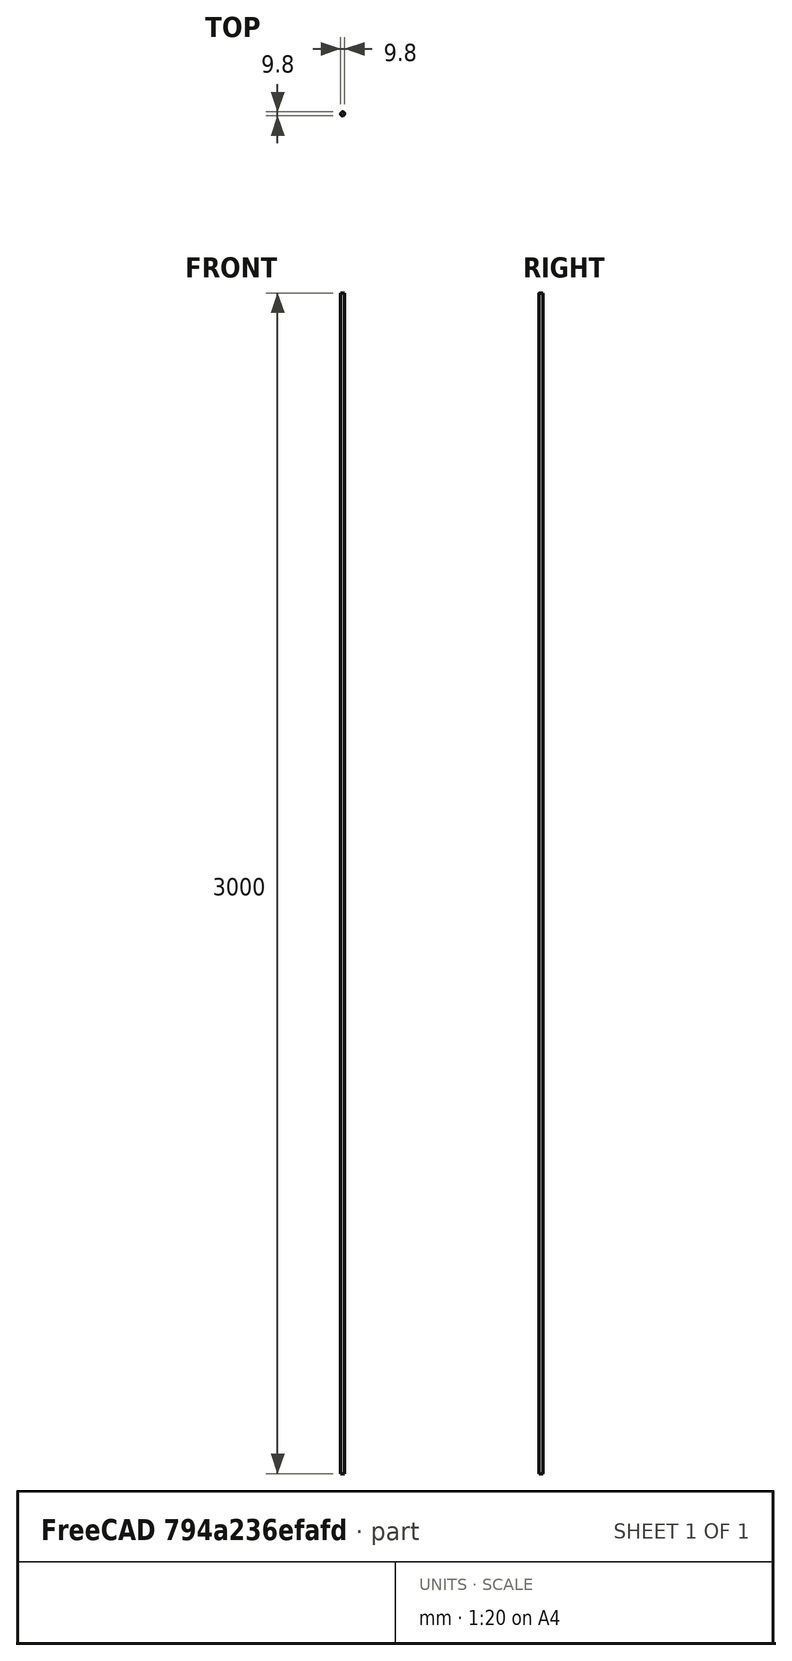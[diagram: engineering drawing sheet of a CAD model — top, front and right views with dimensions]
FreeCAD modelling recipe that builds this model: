
FCSTD DOCUMENT  (FreeCAD 0.21R33771 (Git))
Label: longFuel
License: All rights reserved
LicenseURL: http://en.wikipedia.org/wiki/All_rights_reserved
objects: Part::FeaturePython×5, App::DocumentObjectGroupPython×2, Sketcher::SketchObject×1, PartDesign::Pad×1, PartDesign::Body×1, App::MaterialObjectPython×1, Fem::FemMeshObject×1
note: 9 computed .brp shape members not serialized (recipe doc carries the construction recipe); baked Part::Feature solids carry a one-line shape summary decoded from their .brp

FEATURE [Sketcher::SketchObject] Sketch
  FullyConstrained = true
  MapMode = 5
  Support = -> [XY_Plane]
  sketch-geometry (1):
    g0: Circle CenterX=0 CenterY=0 CenterZ=0 NormalX=0 NormalY=0 NormalZ=1 AngleXU=0 Radius=4.9
  constraints (2):
    c: Coincident(g0,g-1)
    c: Diameter(g0) = 9.8
FEATURE [PartDesign::Pad] Pad
  Direction = (0,0,1)
  Length = 3000
  Length2 = 10
  Profile = -> Sketch
  ReferenceAxis = -> Sketch [N_Axis]
  Type = 0
FEATURE [PartDesign::Body] Body
  Group = -> [Sketch,Pad]
  Origin = -> Origin
  Tip = -> Pad
FEATURE [Part::FeaturePython] PhysicsModel  # WARN: FeaturePython — macro-defined, semantics opaque (R4)
  Flow = 1
  Phase = 0
  SRFModelAxis = (0,0,0)
  SRFModelCoR = (0,0,0)
  SRFModelEnabled = false
  SRFModelRPM = 0
  Time = 0
  Turbulence = 1
  TurbulenceModel = 0
  gx = 0
  gy = 0
  gz = -9800
FEATURE [App::MaterialObjectPython] FluidProperties  label="Air"  # material (typed FeaturePython)
  Category = 1
  Material = CardName=AirCompressible; Cp=1004.703 J/kg/K; Description=Compressible air properties; MolarMass=0.0289643897748887 kg/mol; Name=Air; SutherlandRefTemperature=273.15 K; SutherlandRefViscosity=1.716e-5 kg/m/s; SutherlandTemperature=110.4 K; Type=Compressible
FEATURE [Part::FeaturePython] InitialiseFields  # WARN: FeaturePython — macro-defined, semantics opaque (R4)
  PotentialFlow = false
  PotentialFlowP = false
  Pressure = 100
  ReThetat = 1
  Temperature = 800
  UseInletTemperatureValue = false
  UseInletTurbulenceValues = false
  UseInletUValues = false
  UseOutletPValue = false
  Ux = 0
  Uy = 0
  Uz = 0
  epsilon = 50000000
  gammaInt = 1
  k = 10000
  nuTilda = 55000000
  nut = 50000000
  omega = 1
FEATURE [Part::FeaturePython] CfdSolver  # WARN: FeaturePython — macro-defined, semantics opaque (R4)
  ConvergenceTol = 0.001
  EndTime = 1
  InputCaseName = case
  MaxCFLNumber = 5
  MaxInterfaceCFLNumber = 5
  MaxIterations = 2000
  Parallel = true
  ParallelCores = 4
  PurgeWrite = 0
  StartFrom = 0
  SteadyWriteInterval = 100
  TimeStep = 0.001
  TransientWriteInterval = 0.1
FEATURE [Part::FeaturePython] CfdFluidBoundary001  label="endCaps"  # WARN: FeaturePython — macro-defined, semantics opaque (R4)
  BoundarySubType = 0
  BoundaryType = 0
  DefaultBoundary = false
  DissipationRate = 50000000
  HeatFlux = 0
  HeatTransferCoeff = 0
  Intermittency = 1
  MassFlowRate = 0
  NuTilda = 55000000
  PeriodicCentreOfRotation = (0,0,0)
  PeriodicCentreOfRotationAxis = (0,0,0)
  PeriodicMaster = true
  PeriodicSeparationVector = (0,0,0)
  PorousBaffleMethod = 0
  Pressure = 100
  PressureDropCoeff = 0
  ReThetat = 1
  RelativeToFrame = false
  ReverseNormal = false
  RotationalPeriodic = false
  RoughnessConstant = 0.5
  RoughnessHeight = 0
  ScreenSpacing = 2
  ScreenWireDiameter = 0.2
  ShapeRefs = -> [Pad]
  SlipRatio = 0
  SpecificDissipationRate = 1
  Temperature = 290
  ThermalBoundaryType = 1
  TurbulenceInletSpecification = 2
  TurbulenceIntensityPercentage = 1
  TurbulenceLengthScale = 100
  TurbulentKineticEnergy = 10000
  TurbulentViscosity = 50000000
  Ux = 0
  Uy = 0
  Uz = 0
  VelocityIsCartesian = true
  VelocityMag = 0
  VolFlowRate = 0
  kEqnTurbulentKineticEnergy = 10000
  kEqnTurbulentViscosity = 50000000
FEATURE [Part::FeaturePython] CfdFluidBoundary  label="circularWall"  # WARN: FeaturePython — macro-defined, semantics opaque (R4)
  BoundarySubType = 0
  BoundaryType = 0
  DefaultBoundary = false
  DissipationRate = 50000000
  HeatFlux = 220000
  HeatTransferCoeff = 0
  Intermittency = 1
  MassFlowRate = 0
  NuTilda = 55000000
  PeriodicCentreOfRotation = (0,0,0)
  PeriodicCentreOfRotationAxis = (0,0,0)
  PeriodicMaster = true
  PeriodicSeparationVector = (0,0,0)
  PorousBaffleMethod = 0
  Pressure = 100
  PressureDropCoeff = 0
  ReThetat = 1
  RelativeToFrame = false
  ReverseNormal = false
  RotationalPeriodic = false
  RoughnessConstant = 0.5
  RoughnessHeight = 0
  ScreenSpacing = 2
  ScreenWireDiameter = 0.2
  ShapeRefs = -> [Pad]
  SlipRatio = 0
  SpecificDissipationRate = 1
  Temperature = 290
  ThermalBoundaryType = 2
  TurbulenceInletSpecification = 2
  TurbulenceIntensityPercentage = 1
  TurbulenceLengthScale = 100
  TurbulentKineticEnergy = 10000
  TurbulentViscosity = 50000000
  Ux = 0
  Uy = 0
  Uz = 0
  VelocityIsCartesian = true
  VelocityMag = 0
  VolFlowRate = 0
  kEqnTurbulentKineticEnergy = 10000
  kEqnTurbulentViscosity = 50000000
FEATURE [Fem::FemMeshObject] Pad_MeshSurfaceMesh
FEATURE [App::DocumentObjectGroupPython] Pad_Mesh  # scripted group (container) (typed FeaturePython)
  CaseName = meshCase
  CellsBetweenLevels = 3
  CharacteristicLengthMax = 0.5
  ConvertToDualMesh = false
  EdgeRefinement = 1
  ElementDimension = 1
  Group = -> [Pad_MeshSurfaceMesh]
  ImplicitEdgeDetection = false
  MeshUtility = 0
  NumberOfProcesses = 1
  NumberOfThreads = 0
  Part = -> Pad
  PointInMesh = x=0 m; y=0 m; z=0 m
  STLAngularMeshDensity = 100
  STLRelativeLinearDeflection = 0.001
FEATURE [App::DocumentObjectGroupPython] CfdAnalysis  # scripted group (container) (typed FeaturePython)
  Group = -> [PhysicsModel,FluidProperties,InitialiseFields,CfdSolver,CfdFluidBoundary001,CfdFluidBoundary,Pad_Mesh]
  HostfileName = ../mpi_hostfile
  IsActiveAnalysis = true
  NeedsCaseRewrite = true
  NeedsMeshRerun = false
  NeedsMeshRewrite = true
  UseHostfile = false
